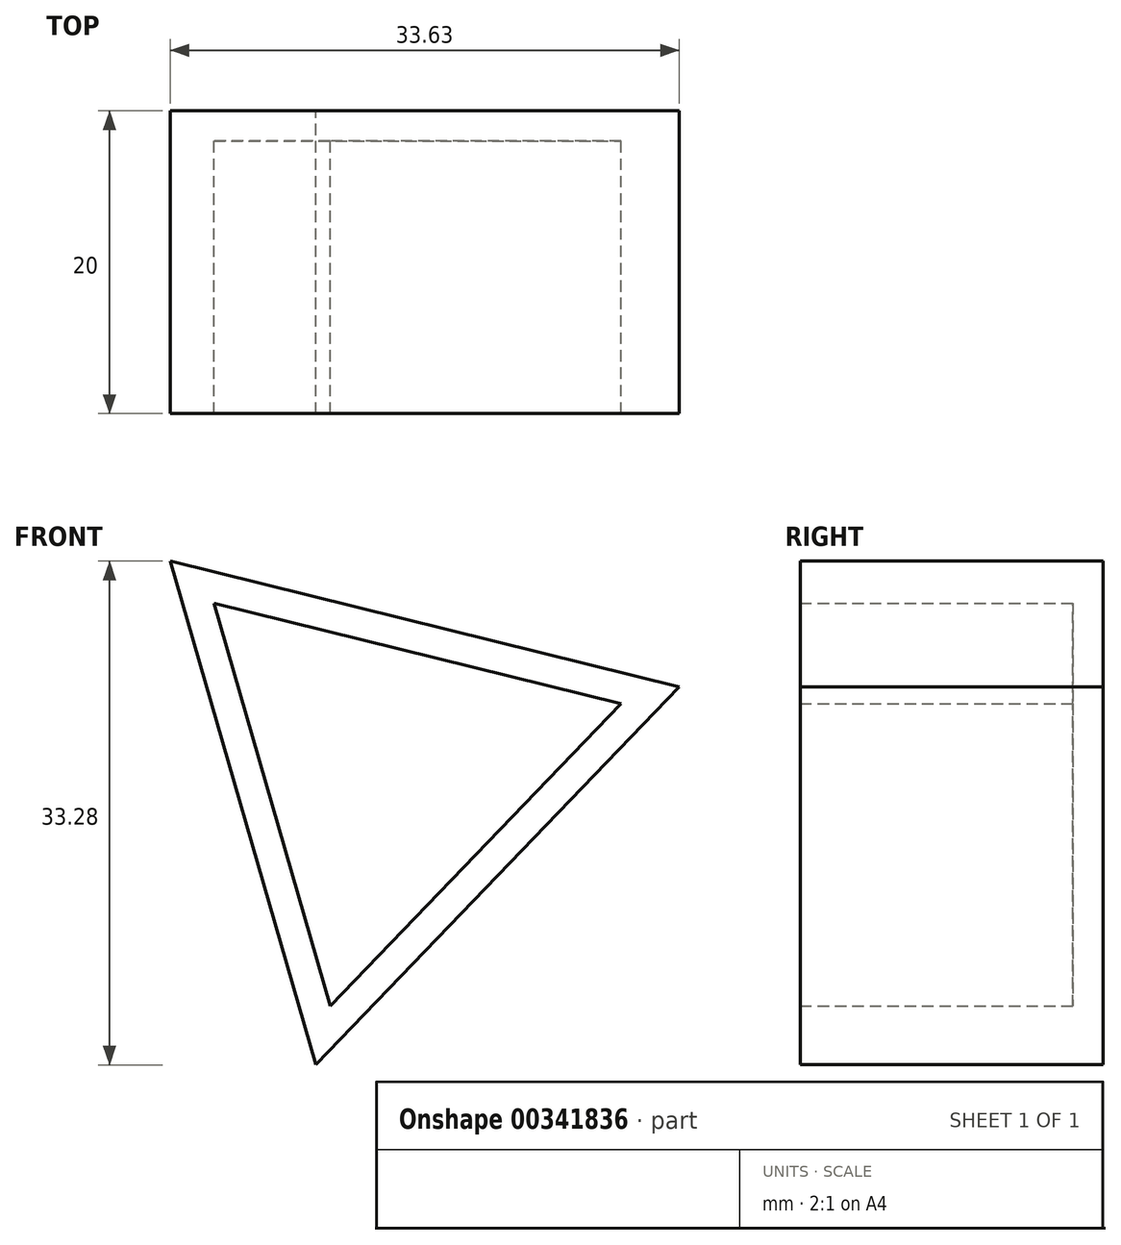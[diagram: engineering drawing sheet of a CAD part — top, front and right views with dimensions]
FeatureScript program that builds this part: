
annotation { "Feature Type Name" : "Feature", "Feature Type Description" : "" }
export const myFeature = defineFeature(function(context is Context, id is Id, definition is map)
    precondition{}
    {
        {
            var Q0;
            Q0=qCreatedBy(makeId("Front.planeOp"),FACE);
            var sketch = newSketch(context, id + "F0", { "sketchPlane" : qUnion([Q0])});
            skCircle(sketch, "E0.cCircle", {"center": v(0, 0) * mm, "radius": 10 * mm, "construction": true});
            skLineSegment(sketch, "E0.0", {"start": v(19.21, 5.55) * mm, "end": v(-4.8, -19.42) * mm});
            skLineSegment(sketch, "E0.1", {"start": v(-4.8, -19.42) * mm, "end": v(-14.42, 13.86) * mm});
            skLineSegment(sketch, "E0.2", {"start": v(-14.42, 13.86) * mm, "end": v(19.21, 5.55) * mm});
            skPoint(sketch, "E0.0.midPoint", {"position": v(7.2, -6.93) * mm});
            skSolve(sketch);
        }
        {
            var Q0;
            Q0=makeQuery(id+"F0.imprint","IMPRINT",FACE,{"disambiguationData":[TD([[makeQuery(id+"F0.imprint","IMPRINT",EDGE,{"derivedFrom":sQuery(id+"F0.wireOp",EDGE,"E0.0")}),-1.0]])]});
            extrude(context, id + "F1", {"entities" : qUnion([Q0]), "depth" : 20 * mm});
        }
        {
            var Q0;
            Q0=makeQuery(id+"F1.opExtrude","CAP_FACE",FACE,{"disambiguationData":[OSD([sQuery(id+"F0.wireOp",EDGE,"E0.0"),sQuery(id+"F0.wireOp",EDGE,"E0.1"),sQuery(id+"F0.wireOp",EDGE,"E0.2")])],"isStart":false});
            shell(context, id + "F2", {"entities" : qUnion([Q0]), "thickness" : 2 * mm});
        }
    });
